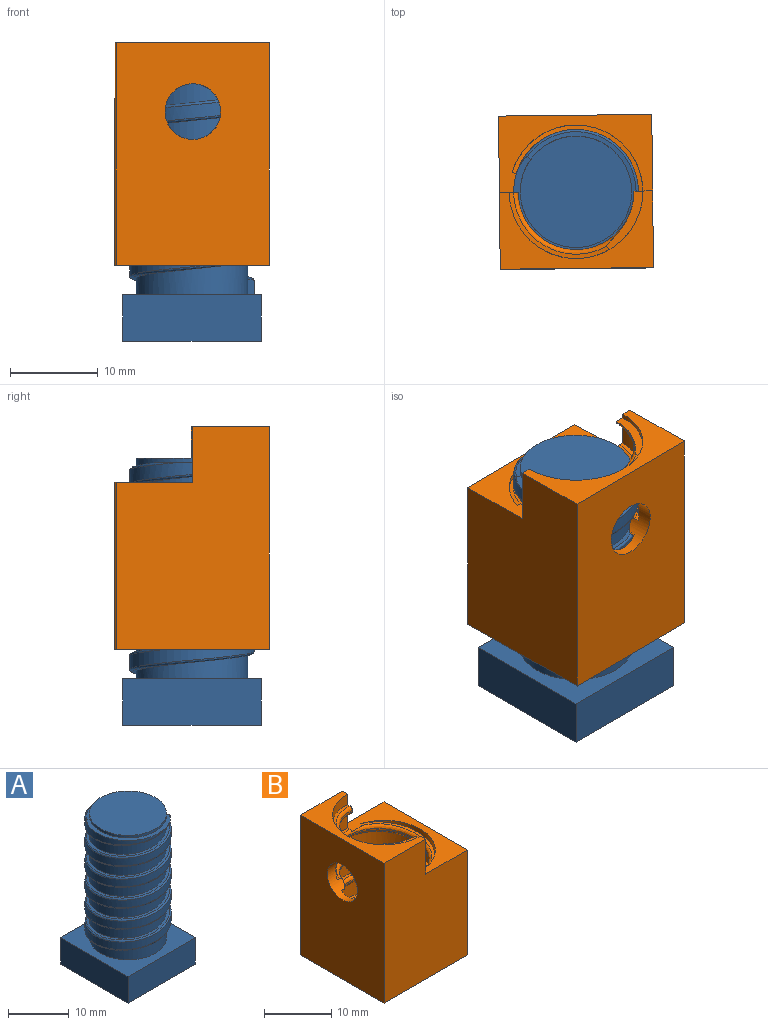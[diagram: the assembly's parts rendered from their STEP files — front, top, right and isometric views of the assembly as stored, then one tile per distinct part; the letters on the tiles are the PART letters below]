
ASSEMBLY  parts=2 mates=1
PART A: 20 faces, bbox 15.9x16.6x30.7 mm
  f0: cylinder r=7.11mm len=24.64mm, axis (0,0,1), area 382.1mm2, adj f8,f11,f18,f19
  f1: bspline ~25.4x16.42mm, area 123.3mm2, adj f2,f3,f4,f5,f6,f7,f11,f16
  f2: cylinder r=6.35mm len=12.7mm, axis (0,0,-1), area 120.4mm2, adj f1,f7,f9,f10,f11
  f3: cylinder r=6.35mm len=12.7mm, axis (0,0,-1), area 74.5mm2, adj f1,f4,f8,f16
  f4: cylinder r=6.35mm len=12.7mm, axis (0,0,-1), area 87.8mm2, adj f1,f3,f5,f9
  f5: cylinder r=6.35mm len=12.7mm, axis (0,0,-1), area 87.8mm2, adj f1,f4,f6,f9
  f6: cylinder r=6.35mm len=12.7mm, axis (0,0,-1), area 87.9mm2, adj f1,f5,f7,f9
  f7: cylinder r=6.35mm len=12.7mm, axis (0,0,-1), area 87.8mm2, adj f1,f2,f6,f9
  f8: plane 1.79x0.77mm, normal (0,-1,0), area 1.3mm2, adj f0,f3,f9,f16,f18,f19
  f9: bspline ~23.28x16.42mm, area 114.4mm2, adj f2,f4,f5,f6,f7,f8,f11,f19
  f10: plane 12.7x12.7mm, normal (0,0,1), area 126.7mm2, adj f2
  f11: plane 12.34x11.3mm, normal (0,0,1), area 15.2mm2, adj f0,f1,f2,f9,f18,f19
  f12: plane 15.75x5.33mm, normal (1,0,0), area 84mm2, adj f13,f15,f16,f17
  f13: plane 15.75x5.33mm, normal (0,-1,0), area 84mm2, adj f12,f14,f16,f17
  f14: plane 15.75x5.33mm, normal (-1,0,0), area 84mm2, adj f13,f15,f16,f17
  f15: plane 15.75x5.33mm, normal (0,1,0), area 84mm2, adj f12,f14,f16,f17
  f16: plane 15.75x15.75mm, normal (0,0,1), area 119.5mm2, adj f1,f3,f8,f12,f13,f14,f15,f18
  f17: plane 15.75x15.75mm, normal (0,0,-1), area 248mm2, adj f12,f13,f14,f15
  f18: bspline ~25.22x14.25mm, area 102.9mm2, adj f0,f1,f8,f11,f16
  f19: bspline ~23.46x14.25mm, area 96.1mm2, adj f0,f8,f9,f11
PART B: 37 faces, bbox 17.9x18x25.9 mm
  f0: bspline ~11.43x8.8mm, area 5.2mm2, adj f7,f10,f33,f36
  f1: bspline ~15.4x11.43mm, area 7.8mm2, adj f6,f11,f18,f35
  f2: bspline ~11.43x8.8mm, area 5mm2, adj f7,f9,f33,f35
  f3: bspline ~17.6x15.24mm, area 15mm2, adj f8,f9,f33,f34
  f4: bspline ~11.43x8.8mm, area 4.5mm2, adj f8,f20,f33,f36
  f5: bspline ~17.6x11.43mm, area 11.8mm2, adj f7,f19,f35,f36
  f6: cylinder r=7.62mm len=15.24mm, axis (0,0,-1), area 23.2mm2, adj f1,f17,f18,f35,f36
  f7: cylinder r=7.62mm len=15.24mm, axis (0,0,-1), area 70.9mm2, adj f0,f2,f5,f33,f35,f36
  f8: cylinder r=7.62mm len=14.89mm, axis (0,0,-1), area 46.9mm2, adj f3,f4,f33,f34,f36
  f9: bspline ~14.23x14.21mm, area 29.7mm2, adj f2,f3,f22,f33,f34,f35
  f10: bspline ~8.6x7.31mm, area 7.2mm2, adj f0,f13,f33,f36
  f11: bspline ~14.17x8.29mm, area 13.3mm2, adj f1,f12,f18,f35
  f12: cylinder r=6.6mm len=13.21mm, axis (0,0,1), area 4.9mm2, adj f11,f18,f19,f35,f36
  f13: cylinder r=6.6mm len=6.3mm, axis (0,0,1), area 2mm2, adj f10,f20,f33,f36
  f14: plane 19.05x17.48mm, normal (1,0,0), area 332.9mm2, adj f15,f16,f30,f34
  f15: plane 25.4x17.48mm, normal (0,1,0), area 388.4mm2, adj f14,f17,f29,f30,f34,f35
  f16: plane 25.4x17.48mm, normal (0,-1,0), area 388.4mm2, adj f14,f17,f29,f30,f34,f36
  f17: plane 17.48x8.74mm, normal (0,0,1), area 61.5mm2, adj f6,f15,f16,f29,f35,f36
  f18: plane 7.06x4.58mm, normal (0,0,1), area 7.2mm2, adj f1,f6,f11,f12,f36
  f19: bspline ~14.23x8.72mm, area 17.1mm2, adj f5,f12,f35,f36
  f20: bspline ~7.53x6mm, area 6.6mm2, adj f4,f13,f33,f36
  f21: bspline ~17.6x15.24mm, area 21.1mm2, adj f25,f28,f33
  f22: cylinder r=6.6mm len=13.21mm, axis (0,0,1), area 9mm2, adj f9,f25,f33
  f23: cylinder r=6.6mm len=14.83mm, axis (0,0,1), area 34.1mm2, adj f24,f31,f32,f33
  f24: bspline ~15.32x14.25mm, area 118.3mm2, adj f23,f27,f31,f33
  f25: bspline ~14.24x14.06mm, area 30.1mm2, adj f21,f22,f33
  f26: bspline ~17.6x15.24mm, area 81.4mm2, adj f28,f31,f32,f33
  f27: bspline ~17.6x15.24mm, area 81.8mm2, adj f24,f28,f31,f33
  f28: cylinder r=7.62mm len=18.79mm, axis (0,0,-1), area 585.7mm2, adj f21,f26,f27,f30,f31,f33
  f29: plane 25.4x17.48mm, normal (-1,0,0), area 412.2mm2, adj f15,f16,f17,f30,f33
  f30: plane 17.48x17.48mm, normal (0,0,-1), area 123mm2, adj f14,f15,f16,f28,f29
  f31: plane 1.29x1.04mm, normal (0,-1,0), area 1.2mm2, adj f23,f24,f26,f27,f28,f32
  f32: bspline ~15.28x14.24mm, area 117.5mm2, adj f23,f26,f31,f33
  f33: cylinder r=3.17mm len=6.35mm, axis (1,0,0), area 35.4mm2, adj f0,f2,f3,f4,f7,f8,f9,f10
  f34: plane 17.71x8.97mm, normal (0,0,1), area 63.2mm2, adj f3,f8,f9,f14,f15,f16,f35,f36
  f35: plane 6.38x2.16mm, normal (1,0,0), area 8.4mm2, adj f1,f2,f5,f6,f7,f9,f11,f12
  f36: plane 6.38x2.16mm, normal (1,0,0), area 8.8mm2, adj f0,f4,f5,f6,f7,f8,f10,f12
PLACE A at identity fixed
PLACE B rot(axis=(0,0,1),90.6deg) t=(0,0,3.6)mm
MATE revolute B.f6 <-> A.f0  axis (0,0,-1) through (0,0,25.4)mm
